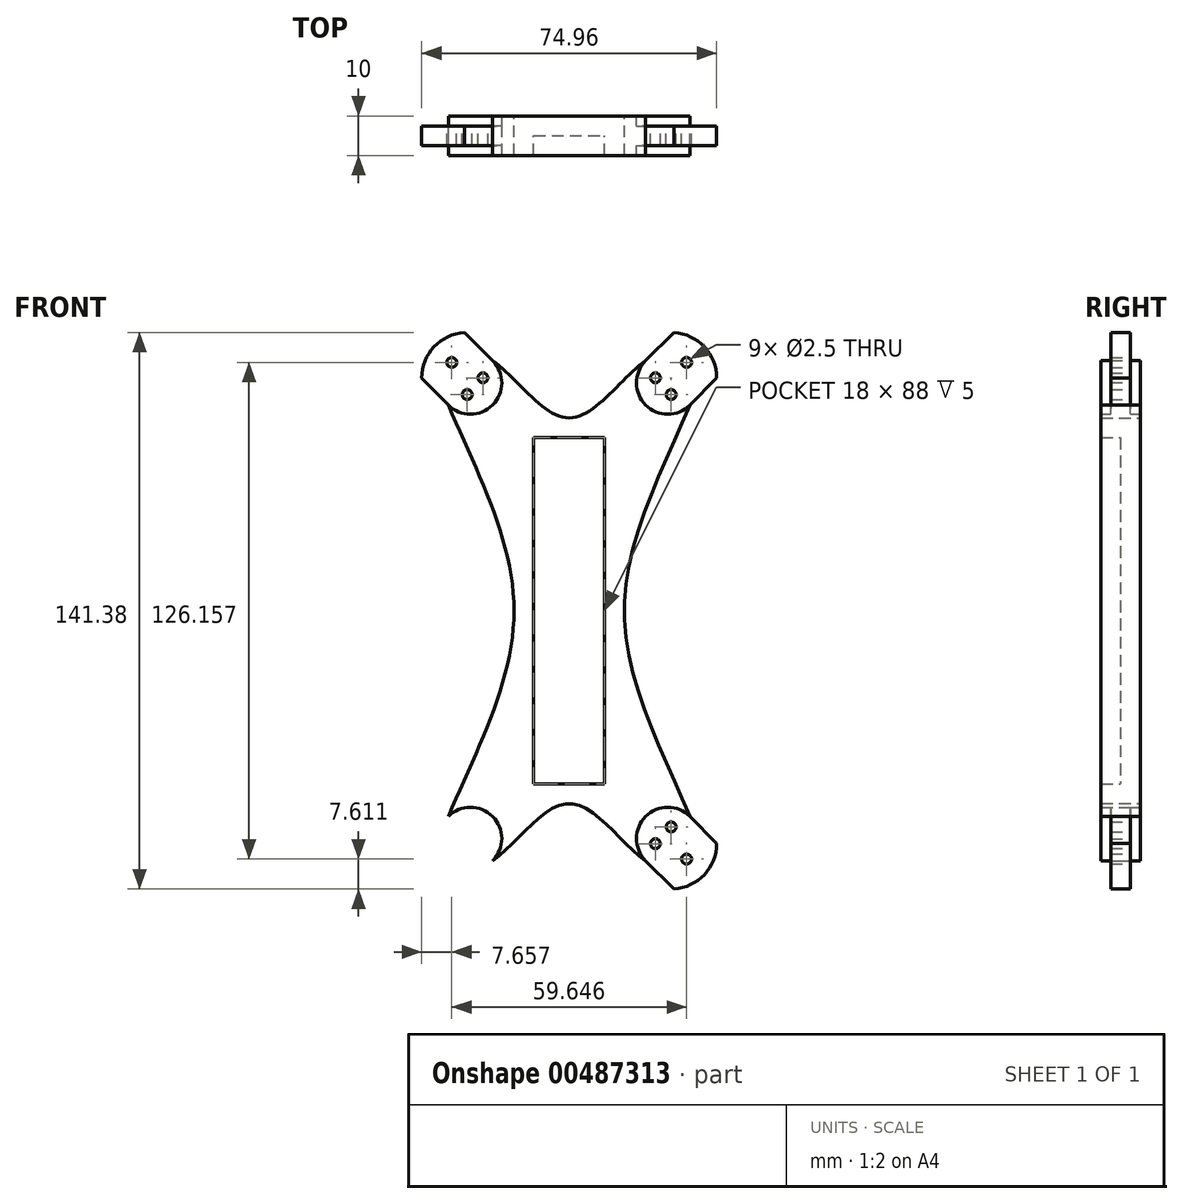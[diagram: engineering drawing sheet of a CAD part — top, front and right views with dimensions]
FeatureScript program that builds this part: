
annotation { "Feature Type Name" : "Feature", "Feature Type Description" : "" }
export const myFeature = defineFeature(function(context is Context, id is Id, definition is map)
    precondition{}
    {
        {
            var Q0;
            Q0=qCreatedBy(makeId("Front.planeOp"),FACE);
            var sketch = newSketch(context, id + "F0", { "sketchPlane" : qUnion([Q0])});
            skPoint(sketch, "E0.middle", {"position": v(0, 0) * mm});
            skLineSegment(sketch, "E1.bottom", {"start": v(-9, 44) * mm, "end": v(9, 44) * mm});
            skLineSegment(sketch, "E1.top", {"start": v(-9, -44) * mm, "end": v(9, -44) * mm});
            skLineSegment(sketch, "E1.left", {"start": v(-9, 44) * mm, "end": v(-9, -44) * mm});
            skLineSegment(sketch, "E1.right", {"start": v(9, 44) * mm, "end": v(9, -44) * mm});
            skPoint(sketch, "E2.visualSharp", {"position": v(-37.17, 70.4) * mm});
            skArc(sketch, "E2.filletArc", {"start": v(-26.6, 70.7) * mm, "mid": v(-34.33, 67.07) * mm, "end": v(-37.48, 59.14) * mm});
            skPoint(sketch, "E3.visualSharp", {"position": v(37.17, 70.4) * mm});
            skArc(sketch, "E3.filletArc", {"start": v(37.48, 59.14) * mm, "mid": v(34.1, 67.32) * mm, "end": v(25.9, 70.71) * mm});
            skPoint(sketch, "E4.visualSharp", {"position": v(37.17, -70.4) * mm});
            skArc(sketch, "E4.filletArc", {"start": v(25.9, -70.71) * mm, "mid": v(34.1, -67.32) * mm, "end": v(37.48, -59.14) * mm});
            skPoint(sketch, "E5.visualSharp", {"position": v(-37.17, -70.4) * mm});
            skArc(sketch, "E5.filletArc", {"start": v(-37.48, -59.14) * mm, "mid": v(-34.1, -67.32) * mm, "end": v(-25.9, -70.71) * mm});
            skLineSegment(sketch, "E6", {"start": v(-37.48, 59.14) * mm, "end": v(-30.7, 52.26) * mm});
            skLineSegment(sketch, "E7", {"start": v(-26.6, 70.7) * mm, "end": v(-19.44, 63.52) * mm});
            skArc(sketch, "E8", {"start": v(-30.7, 52.26) * mm, "mid": v(-19.44, 52.26) * mm, "end": v(-19.44, 63.52) * mm});
            skLineSegment(sketch, "E9.MirrorCS", {"start": v(26.6, 70.7) * mm, "end": v(19.44, 63.52) * mm});
            skLineSegment(sketch, "E10.MirrorCS", {"start": v(37.48, 59.14) * mm, "end": v(30.7, 52.26) * mm});
            skArc(sketch, "E11.MirrorCS", {"start": v(30.7, 52.26) * mm, "mid": v(19.44, 52.26) * mm, "end": v(19.44, 63.52) * mm});
            skArc(sketch, "E12.MirrorCS", {"start": v(-26.6, -70.7) * mm, "mid": v(-34.33, -67.07) * mm, "end": v(-37.48, -59.14) * mm});
            skLineSegment(sketch, "E13.MirrorCS", {"start": v(-26.6, -70.7) * mm, "end": v(-19.44, -63.52) * mm});
            skLineSegment(sketch, "E14.MirrorCS", {"start": v(-37.48, -59.14) * mm, "end": v(-30.7, -52.26) * mm});
            skArc(sketch, "E15.MirrorCS", {"start": v(-30.7, -52.26) * mm, "mid": v(-19.44, -52.26) * mm, "end": v(-19.44, -63.52) * mm});
            skLineSegment(sketch, "E16.MirrorCS", {"start": v(37.48, -59.14) * mm, "end": v(30.7, -52.26) * mm});
            skArc(sketch, "E17.MirrorCS", {"start": v(30.7, -52.26) * mm, "mid": v(19.44, -52.26) * mm, "end": v(19.44, -63.52) * mm});
            skLineSegment(sketch, "E18.MirrorCS", {"start": v(26.6, -70.7) * mm, "end": v(19.44, -63.52) * mm});
            skLineSegment(sketch, "E19", {"start": v(-9, 0) * mm, "end": v(-14, 0) * mm});
            skLineSegment(sketch, "E20", {"start": v(0, 44) * mm, "end": v(0, 49) * mm});
            skPoint(sketch, "E20.endSnap0", {"position": v(0, 44) * mm});
            skFitSpline(sketch, "E21", {"points": [v(-30.7, -52.26) * mm, v(-14, 0) * mm, v(-30.7, 52.26) * mm], "startDerivative": vector(44.6, 103.94) * mm, "endDerivative": vector(-44.6, 103.94) * mm});
            skFitSpline(sketch, "E22", {"points": [v(-19.44, 63.52) * mm, v(0, 49) * mm, v(19.44, 63.52) * mm], "startDerivative": vector(37.48, -26.01) * mm, "endDerivative": vector(37.48, 26.01) * mm});
            skFitSpline(sketch, "E23.MirrorCS", {"points": [v(30.7, -52.26) * mm, v(14, 0) * mm, v(30.7, 52.26) * mm], "startDerivative": vector(-44.6, 103.94) * mm, "endDerivative": vector(44.6, 103.94) * mm});
            skFitSpline(sketch, "E24.MirrorCS", {"points": [v(-19.44, -63.52) * mm, v(0, -49) * mm, v(19.44, -63.52) * mm], "startDerivative": vector(37.48, 26.01) * mm, "endDerivative": vector(37.48, -26.01) * mm});
            skCircle(sketch, "E25", {"center": v(-29.82, 63.08) * mm, "radius": 1.25 * mm});
            skCircle(sketch, "E26", {"center": v(-21.9, 59.19) * mm, "radius": 1.25 * mm});
            skCircle(sketch, "E27", {"center": v(-25.9, 54.92) * mm, "radius": 1.25 * mm});
            skCircle(sketch, "E28.MirrorC", {"center": v(29.82, 63.08) * mm, "radius": 1.25 * mm});
            skCircle(sketch, "E29.MirrorC", {"center": v(21.9, 59.19) * mm, "radius": 1.25 * mm});
            skCircle(sketch, "E30.MirrorC", {"center": v(25.9, 54.92) * mm, "radius": 1.25 * mm});
            skCircle(sketch, "E31.MirrorC", {"center": v(25.9, -54.92) * mm, "radius": 1.25 * mm});
            skCircle(sketch, "E32.MirrorC", {"center": v(29.82, -63.08) * mm, "radius": 1.25 * mm});
            skCircle(sketch, "E33.MirrorC", {"center": v(21.9, -59.19) * mm, "radius": 1.25 * mm});
            skCircle(sketch, "E34.MirrorC", {"center": v(-29.82, -63.08) * mm, "radius": 1.25 * mm});
            skCircle(sketch, "E35.MirrorC", {"center": v(-21.9, -59.19) * mm, "radius": 1.25 * mm});
            skCircle(sketch, "E36.MirrorC", {"center": v(-25.9, -54.92) * mm, "radius": 1.25 * mm});
            skLineSegment(sketch, "E37", {"start": v(-29.82, -63.08) * mm, "end": v(-17.4, -50.66) * mm});
            skPoint(sketch, "E38", {"position": v(-19.44, -52.26) * mm});
            skSolve(sketch);
        }
        {
            var Q0;
            {var subQ1=sQuery(id+"F0.wireOp",EDGE,"E8");Q0=makeQuery(id+"F0.imprint","IMPRINT",FACE,{"disambiguationData":[TD([[makeQuery(id+"F0.imprint","IMPRINT",EDGE,{"derivedFrom":subQ1}),-1.0]])]});}
            var Q1;
            {var subQ7=sQuery(id+"F0.wireOp",EDGE,"E1.top");Q1=makeQuery(id+"F0.imprint","IMPRINT",FACE,{"disambiguationData":[TD([[makeQuery(id+"F0.imprint","IMPRINT",EDGE,{"derivedFrom":subQ7}),-1.0]])]});}
            extrude(context, id + "F1", {"entities" : qUnion([Q0, Q1]), "endBound" : BoundingType.SYMMETRIC, "depth" : 10 * mm});
        }
        {
            var Q0;
            {var subQ4=sQuery(id+"F0.wireOp",EDGE,"E1.top");Q0=makeQuery(id+"F0.imprint","IMPRINT",FACE,{"disambiguationData":[TD([[makeQuery(id+"F0.imprint","IMPRINT",EDGE,{"derivedFrom":subQ4}),1.0]])]});}
            extrude(context, id + "F2", {"entities" : qUnion([Q0]), "operationType" : NewBodyOperationType.ADD, "oppositeDirection" : true, "depth" : 5 * mm});
        }
        {
            var Q0;
            Q0=makeQuery(id+"F0.imprint","IMPRINT",FACE,{"disambiguationData":[TD([[makeQuery(id+"F0.imprint","IMPRINT",EDGE,{"derivedFrom":sQuery(id+"F0.wireOp",EDGE,"E2.filletArc")}),1.0]])]});
            var Q1;
            Q1=makeQuery(id+"F0.imprint","IMPRINT",FACE,{"disambiguationData":[TD([[makeQuery(id+"F0.imprint","IMPRINT",EDGE,{"derivedFrom":sQuery(id+"F0.wireOp",EDGE,"E3.filletArc")}),1.0]])]});
            var Q2;
            Q2=makeQuery(id+"F0.imprint","IMPRINT",FACE,{"disambiguationData":[TD([[makeQuery(id+"F0.imprint","IMPRINT",EDGE,{"derivedFrom":sQuery(id+"F0.wireOp",EDGE,"E4.filletArc")}),1.0]])]});
            var Q3;
            Q3=makeQuery(id+"F0.imprint","IMPRINT",FACE,{"disambiguationData":[TD([[makeQuery(id+"F0.imprint","IMPRINT",EDGE,{"derivedFrom":sQuery(id+"F0.wireOp",EDGE,"E12.MirrorCS")}),-1.0]])]});
            extrude(context, id + "F3", {"entities" : qUnion([Q0, Q1, Q2, Q3]), "operationType" : NewBodyOperationType.ADD, "endBound" : BoundingType.SYMMETRIC, "depth" : 5 * mm});
        }
    });
